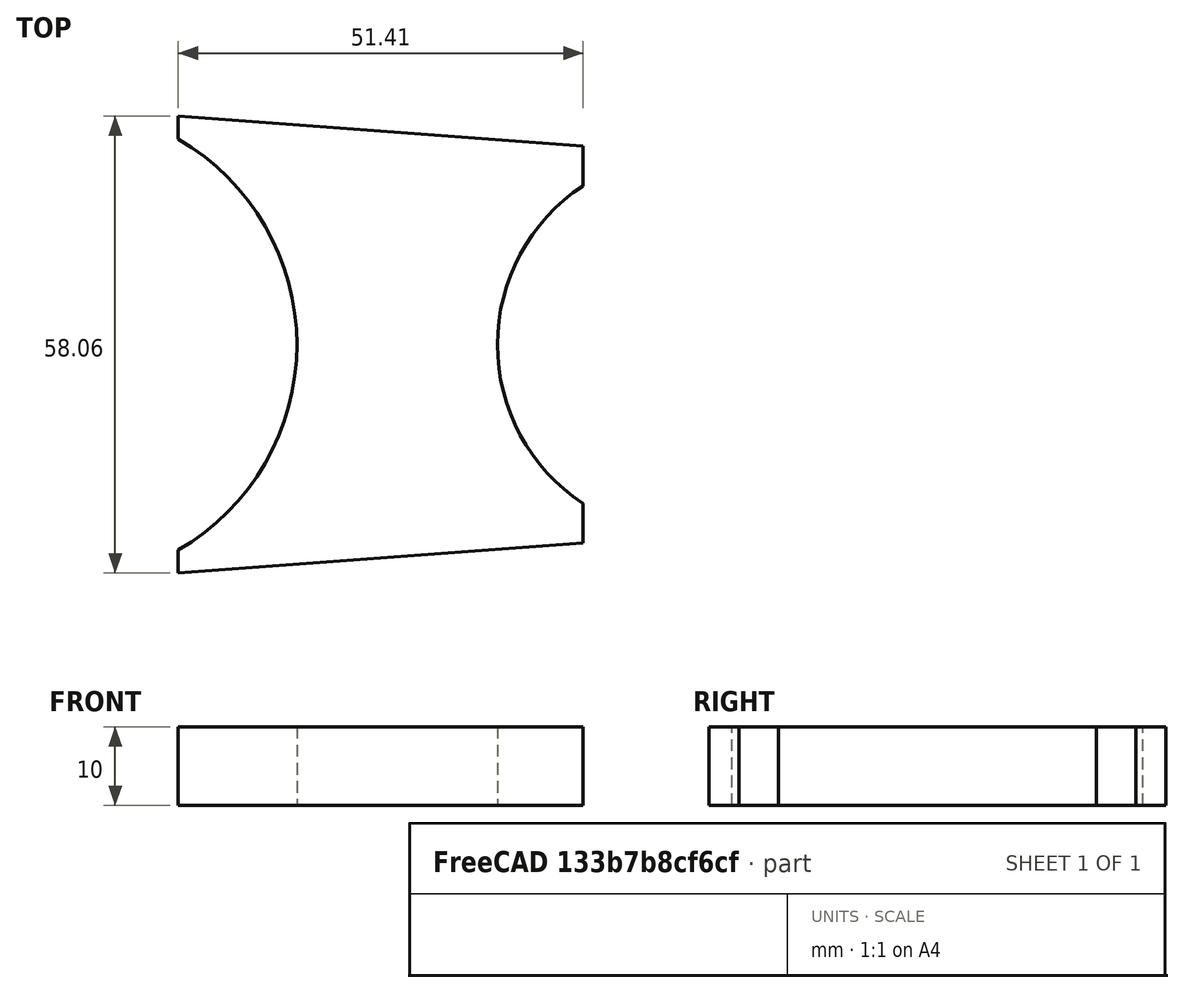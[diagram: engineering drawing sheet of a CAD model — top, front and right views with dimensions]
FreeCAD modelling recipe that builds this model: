
FCSTD DOCUMENT  (FreeCAD 1.0R39109 (Git))
Label: Tail_Hinge_Junction_Cover_Top
License: All rights reserved
LicenseURL: http://en.wikipedia.org/wiki/All_rights_reserved
objects: Sketcher::SketchObject×1, PartDesign::Pad×1, Spreadsheet::Sheet×1, PartDesign::Body×1, TechDraw::DrawSVGTemplate×1, TechDraw::DrawProjGroupItem×1, TechDraw::DrawViewDimension×1, TechDraw::DrawPage×1
note: 8 computed .brp shape members not serialized (recipe doc carries the construction recipe); baked Part::Feature solids carry a one-line shape summary decoded from their .brp
EXTERNAL_REF file=../../../Master_of_Puppets.FCStd obj=Spreadsheet
EXTERNAL_REF file=../../../Master_of_Puppets.FCStd obj=Tail

FEATURE [Sketcher::SketchObject] Sketch
  ArcFitTolerance = 0
  AttachmentSupport = -> [XY_Plane001]
  FullyConstrained = true
  MakeInternals = false
  MapMode = 5
  expr: Constraints[14] = Spreadsheet.Chamfer
  expr: Constraints[16] = Spreadsheet.YawPipeRadius
  expr: Constraints[1] = Spreadsheet.HingeInnerPipeRadius
  expr: Constraints[22] = Spreadsheet.Chamfer
  expr: Constraints[2] = Spreadsheet.FullWidth
  sketch-geometry (14):
    g0: ArcOfCircle [constr] CenterX=79.7779 CenterY=0 CenterZ=0 NormalX=0 NormalY=0 NormalZ=1 AngleXU=0 Radius=24.15 StartAngle=1.49656 EndAngle=4.78663
    g1: Circle [constr] CenterX=0 CenterY=0 CenterZ=0 NormalX=0 NormalY=0 NormalZ=1 AngleXU=0 Radius=30.15
    g2: ArcOfCircle CenterX=0 CenterY=0 CenterZ=0 NormalX=0 NormalY=0 NormalZ=1 AngleXU=0 Radius=30.15 StartAngle=5.23599 EndAngle=7.33038
    g3: LineSegment StartX=15.075 StartY=-26.1107 StartZ=0 EndX=15.075 EndY=-29.0288 EndZ=0
    g4: ArcOfCircle CenterX=79.7779 CenterY=0 CenterZ=0 NormalX=0 NormalY=0 NormalZ=1 AngleXU=0 Radius=24.15 StartAngle=2.15323 EndAngle=4.12996
    g5: LineSegment StartX=66.4941 StartY=-20.1683 StartZ=0 EndX=66.4941 EndY=-25.2047 EndZ=0
    g6: LineSegment [constr] StartX=0 StartY=30.15 StartZ=0 EndX=15.075 EndY=30.15 EndZ=0
    g7: LineSegment [constr] StartX=0 StartY=30.15 StartZ=0 EndX=81.5691 EndY=24.0835 EndZ=0
    g8: LineSegment [constr] StartX=81.5691 StartY=24.0835 StartZ=0 EndX=66.4941 EndY=24.0835 EndZ=0
    g9: LineSegment StartX=15.075 StartY=-29.0288 StartZ=0 EndX=66.4941 EndY=-25.2047 EndZ=0
    g10: LineSegment [constr] StartX=81.5691 StartY=-24.0835 StartZ=0 EndX=0 EndY=-30.15 EndZ=0
    g11: LineSegment StartX=66.4941 StartY=25.2047 StartZ=0 EndX=15.075 EndY=29.0288 EndZ=0
    g12: LineSegment StartX=15.075 StartY=29.0288 StartZ=0 EndX=15.075 EndY=26.1107 EndZ=0
    g13: LineSegment StartX=66.4941 StartY=25.2047 StartZ=0 EndX=66.4941 EndY=20.1683 EndZ=0
  constraints (44):
    c: PointOnObject(g0,g-1)
    c: Radius(g0) = 24.15
    c: DistanceX(g-1,g0) = 79.7779
    c: Coincident(g1,g-1)
    c: Coincident(g2,g1)
    c: PointOnObject(g2,g1)
    c: Vertical(g2,g2)
    c: Coincident(g3,g2)
    c: Vertical(g3)
    c: Coincident(g4,g0)
    c: Coincident(g5,g4)
    c: Vertical(g4,g4)
    c: Vertical(g4,g5)
    c: PointOnObject(g4,g0)
    c: Distance(g6) = 15.075
    c: Vertical(g9,g6)
    c: Radius(g1) = 30.15
    c: PointOnObject(g7,g1)
    c: Coincident(g7,g0)
    c: PointOnObject(g7,g-2)
    c: Coincident(g8,g7)
    c: Horizontal(g8)
    c: Distance(g8) = 15.075
    c: Coincident(g10,g0)
    c: PointOnObject(g10,g-2)
    c: PointOnObject(g10,g1)
    c: Perpendicular(g-2,g6)
    c: Coincident(g6,g7)
    c: Tangent(g10,g0,g0) = 1.5708
    c: Tangent(g0,g7,g7) = 1.5708
    c: PointOnObject(g9,g10)
    c: PointOnObject(g3,g10)
    c: PointOnObject(g9,g10)
    c: PointOnObject(g11,g7)
    c: PointOnObject(g11,g7)
    c: Coincident(g12,g11)
    c: Coincident(g12,g2)
    c: Coincident(g5,g9)
    c: Vertical(g8,g11)
    c: Vertical(g11,g6)
    c: Vertical(g2,g11)
    c: Coincident(g13,g11)
    c: Coincident(g13,g4)
    c: Vertical(g13)
FEATURE [PartDesign::Pad] Pad
  AllowMultiFace = false
  Direction = (0,0,1)
  Length = 10
  Length2 = 100
  Profile = -> Sketch
  Suppressed = false
  Type = 0
  expr: Length = Spreadsheet.FlatMetalThickness
FEATURE [Spreadsheet::Sheet] Spreadsheet
  cells = A1='Inputs; A2='YawPipeDiameter; B2(YawPipeDiameter)==Master_of_Puppets#Spreadsheet.YawPipeDiameter; A3='HingeInnerPipeRadius; B3(HingeInnerPipeRadius)==Master_of_Puppets#Tail.HingeInnerPipeRadius; A4='FlatMetalThickness; B4(FlatMetalThickness)==Master_of_Puppets#Spreadsheet.FlatMetalThickness; A5='FullWidth; B5(FullWidth)==Master_of_Puppets#Tail.TailHingeJunctionFullWidth; A6='Chamfer; B6(Chamfer)==Master_of_Puppets#Tail.TailHingeJunctionChamfer; A7='Calculated; A8='YawPipeRadius; B8(YawPipeRadius)==YawPipeDiameter / 2; A9='XOffset; B9(XOffset)==-Chamfer
FEATURE [PartDesign::Body] PocketBody  label="Tail_Hinge_Junction_Cover_Top"
  AllowCompound = false
  Group = -> [Sketch,Pad]
  Openafpm_Flat = true
  Origin = -> Origin001
  Tip = -> Pad
FEATURE [TechDraw::DrawSVGTemplate] Template
  Height = 210
  Orientation = 1
  Template = <userpath>/micromamba/envs/openafpm-cad-core/share/Mod/TechDraw/Templates/Default_Template_A4_Landscape.svg
  Width = 297
FEATURE [TechDraw::DrawProjGroupItem] View
  CoarseView = false
  Direction = (0,0,1)
  Focus = 100
  HardHidden = false
  IsoCount = 0
  IsoHidden = false
  IsoVisible = false
  LockPosition = false
  Perspective = false
  Rotation = 0
  RotationVector = (1,0,0)
  ScaleType = 0
  ScrubCount = 1
  SeamHidden = false
  SeamVisible = false
  SmoothHidden = false
  SmoothVisible = true
  Source = -> [PocketBody]
  Type = 0
  X = 148.5
  XDirection = (1,0,0)
  Y = 105
FEATURE [TechDraw::DrawViewDimension] Dimension  label="D"
  AngleOverride = false
  Arbitrary = true
  ArbitraryTolerances = false
  BoxCorners = (2) [(-25.7095,-29.0288,0),(25.7095,29.0288,0)]
  EqualTolerance = true
  ExtensionAngle = 0
  FormatSpec = D
  FormatSpecOverTolerance = %+.2w
  FormatSpecUnderTolerance = %+.2w
  Inverted = false
  LineAngle = 0
  LockPosition = false
  MeasureType = 1
  OverTolerance = 0
  References2D = -> [View]
  Rotation = 0
  ScaleType = 0
  TheoreticalExact = false
  Type = 0
  UnderTolerance = 0
  X = 2.10442
  Y = 4.19322
FEATURE [TechDraw::DrawPage] Page
  KeepUpdated = true
  NextBalloonIndex = 1
  ProjectionType = 0
  Template = -> Template
  Views = -> [View,Dimension]
